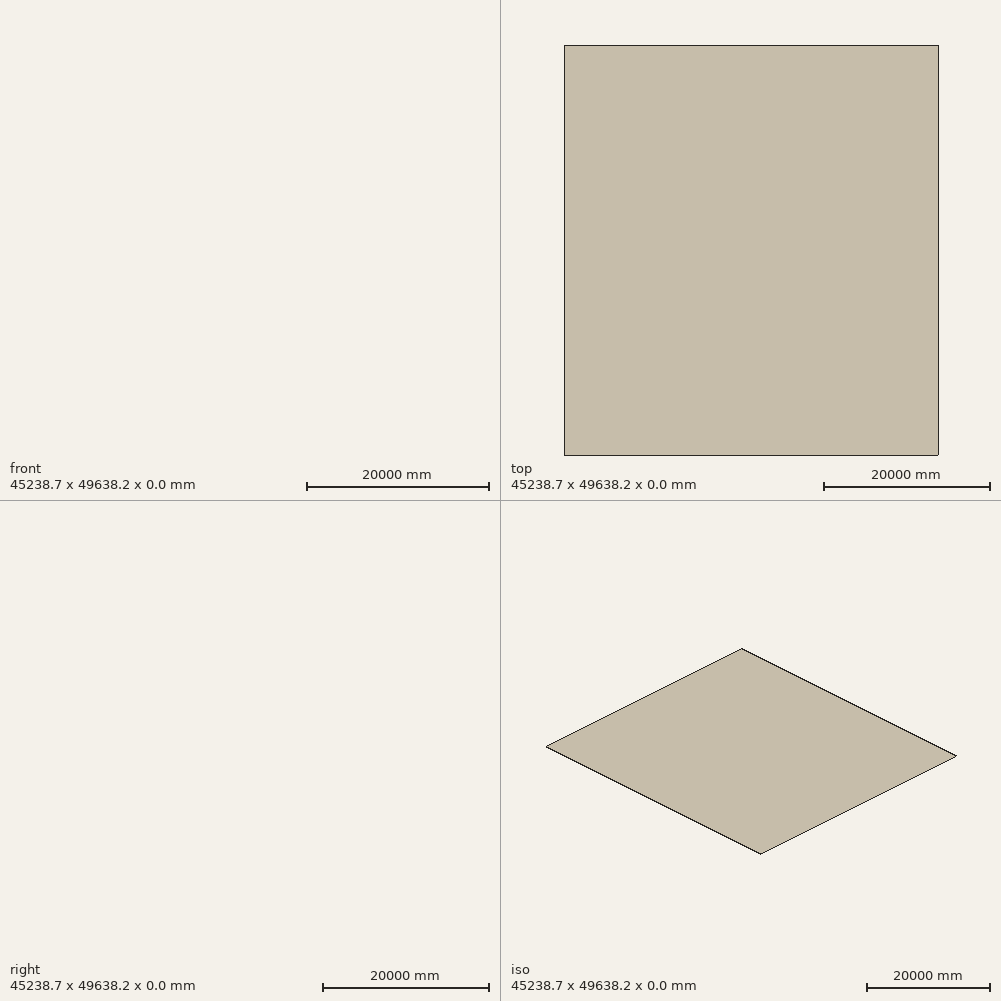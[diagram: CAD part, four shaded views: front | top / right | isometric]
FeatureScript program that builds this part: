
annotation { "Feature Type Name" : "Feature", "Feature Type Description" : "" }
export const myFeature = defineFeature(function(context is Context, id is Id, definition is map)
    precondition{}
    {
        {
            var Q0;
            Q0=qCreatedBy(makeId("Top.planeOp"),FACE);
            var sketch = newSketch(context, id + "F0", { "sketchPlane" : qUnion([Q0])});
            skLineSegment(sketch, "E0.bottom", {"start": v(-6626.25, 7082.55) * mm, "end": v(38612.47, 7082.55) * mm});
            skLineSegment(sketch, "E0.top", {"start": v(-6626.25, -42555.62) * mm, "end": v(38612.47, -42555.62) * mm});
            skLineSegment(sketch, "E0.left", {"start": v(-6626.25, 7082.55) * mm, "end": v(-6626.25, -42555.62) * mm});
            skLineSegment(sketch, "E0.right", {"start": v(38612.47, 7082.55) * mm, "end": v(38612.47, -42555.62) * mm});
            skSolve(sketch);
        }
        {
            var Q0;
            Q0=makeQuery(id+"F0.imprint","IMPRINT",FACE,{"disambiguationData":[TD([[makeQuery(id+"F0.imprint","IMPRINT",EDGE,{"derivedFrom":sQuery(id+"F0.wireOp",EDGE,"E0.bottom")}),-1.0]])]});
            extrude(context, id + "F1", {"entities" : qUnion([Q0]), "depth" : 0.03 * mm});
        }
    });
